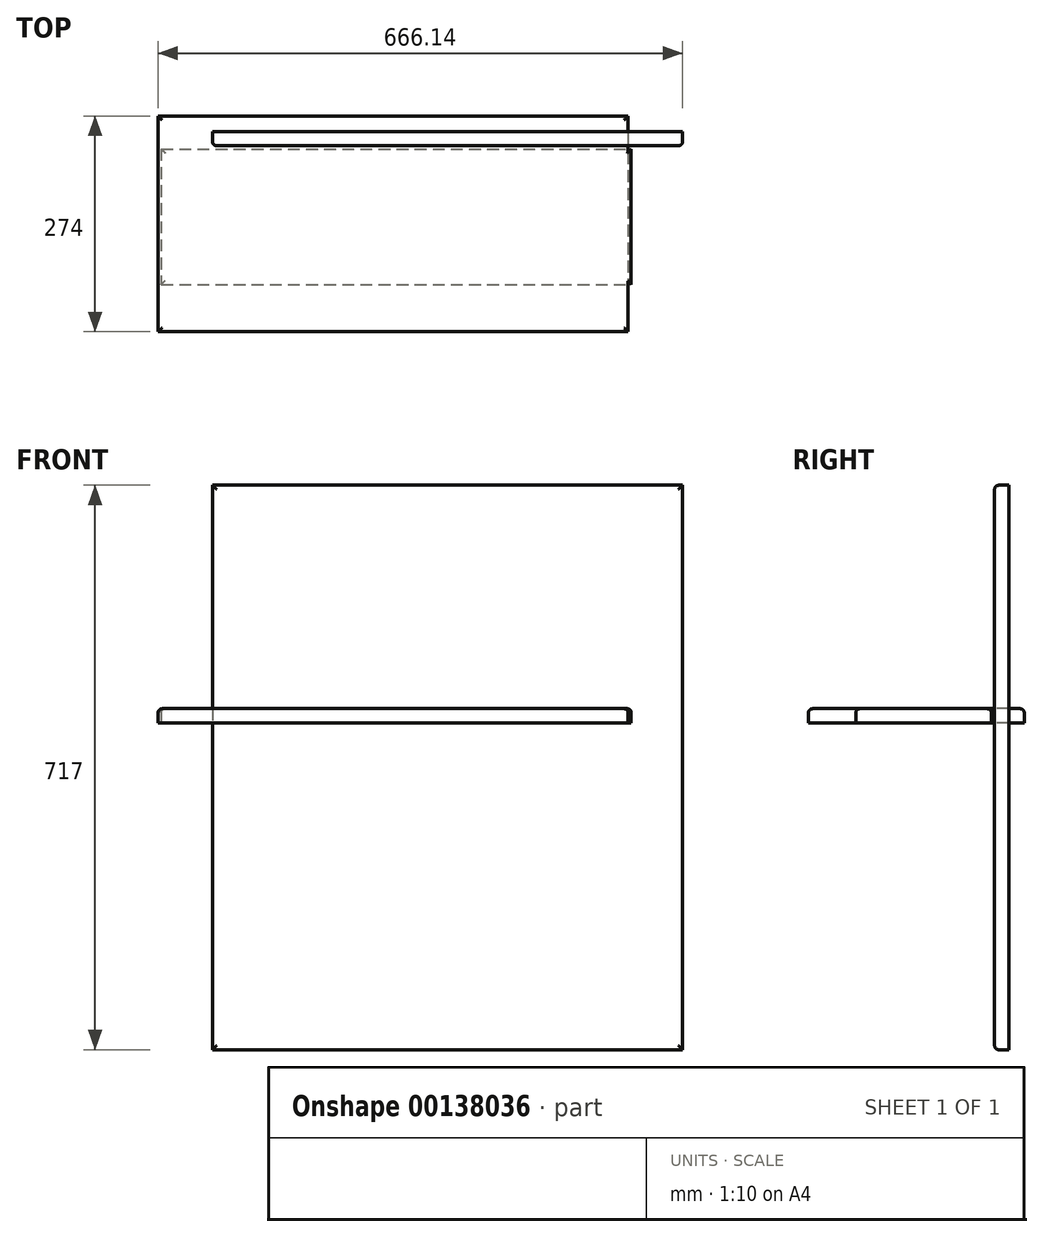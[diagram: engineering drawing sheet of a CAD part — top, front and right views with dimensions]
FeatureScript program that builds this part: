
annotation { "Feature Type Name" : "Feature", "Feature Type Description" : "" }
export const myFeature = defineFeature(function(context is Context, id is Id, definition is map)
    precondition{}
    {
        {
            var Q0;
            Q0=qCreatedBy(makeId("Front.planeOp"),FACE);
            var sketch = newSketch(context, id + "F0", { "sketchPlane" : qUnion([Q0])});
            skLineSegment(sketch, "E0.bottom", {"start": v(-320.4, 301.85) * mm, "end": v(276.6, 301.85) * mm});
            skLineSegment(sketch, "E0.top", {"start": v(-320.4, -415.15) * mm, "end": v(276.6, -415.15) * mm});
            skLineSegment(sketch, "E0.left", {"start": v(-320.4, 301.85) * mm, "end": v(-320.4, -415.15) * mm});
            skLineSegment(sketch, "E0.right", {"start": v(276.6, 301.85) * mm, "end": v(276.6, -415.15) * mm});
            skSolve(sketch);
        }
        {
            var Q0;
            Q0 = qSketchRegion(id + "F0", true);
            extrude(context, id + "F1", {"entities" : qUnion([Q0]), "depth" : 18 * mm});
        }
        {
            var Q0;
            Q0=makeQuery(id+"F1.opExtrude","CAP_FACE",FACE,{"disambiguationData":[OSD([sQuery(id+"F0.wireOp",EDGE,"E0.bottom"),sQuery(id+"F0.wireOp",EDGE,"E0.top"),sQuery(id+"F0.wireOp",EDGE,"E0.left"),sQuery(id+"F0.wireOp",EDGE,"E0.right")])],"isStart":false});
            fillet(context, id + "F2", {"entities" : qUnion([Q0]), "radius" : 5 * mm, "tangentPropagation" : true, "allowEdgeOverflow" : false});
        }
        {
            var Q0;
            Q0=makeQuery(id+"F1.opExtrude","SWEPT_BODY",BODY,{"disambiguationData":[OSD([sQuery(id+"F0.wireOp",EDGE,"E0.bottom"),sQuery(id+"F0.wireOp",EDGE,"E0.top"),sQuery(id+"F0.wireOp",EDGE,"E0.left"),sQuery(id+"F0.wireOp",EDGE,"E0.right")])]});
            transform(context, id + "F3", {"entities" : qUnion([Q0]), "transformType" : TransformType.TRANSLATION_3D, "dx" : 700 * mm, "dy" : 0 * mm, "dz" : 0 * mm, "makeCopy" : true});
        }
        {
            var Q0;
            Q0=makeQuery(id+"F3.opPattern","COPY",FACE,{"derivedFrom":makeQuery(id+"F1.opExtrude","CAP_FACE",FACE,{"disambiguationData":[OSD([sQuery(id+"F0.wireOp",EDGE,"E0.bottom"),sQuery(id+"F0.wireOp",EDGE,"E0.top"),sQuery(id+"F0.wireOp",EDGE,"E0.left"),sQuery(id+"F0.wireOp",EDGE,"E0.right")])],"isStart":false}),"instanceName":"1"});
            var sketch = newSketch(context, id + "F4", { "sketchPlane" : qUnion([Q0])});
            skLineSegment(sketch, "E1.bottom", {"start": v(384.6, 296.85) * mm, "end": v(971.6, 296.85) * mm});
            skLineSegment(sketch, "E1.top", {"start": v(384.6, 124.85) * mm, "end": v(971.6, 124.85) * mm});
            skLineSegment(sketch, "E1.left", {"start": v(384.6, 296.85) * mm, "end": v(384.6, 124.85) * mm});
            skLineSegment(sketch, "E1.right", {"start": v(971.6, 296.85) * mm, "end": v(971.6, 124.85) * mm});
            skSolve(sketch);
        }
        {
            var Q0;
            Q0=makeQuery(id+"F4.imprint","IMPRINT",FACE,{"disambiguationData":[TD([[makeQuery(id+"F4.imprint","IMPRINT",EDGE,{"derivedFrom":sQuery(id+"F4.wireOp",EDGE,"E1.bottom")}),1.0]])]});
            extrude(context, id + "F5", {"entities" : qUnion([Q0]), "operationType" : NewBodyOperationType.ADD, "oppositeDirection" : true, "depth" : 17 * mm});
        }
        {
            var Q0;
            Q0=makeQuery(id+"F3.opPattern","COPY",BODY,{"derivedFrom":makeQuery(id+"F1.opExtrude","SWEPT_BODY",BODY,{"disambiguationData":[OSD([sQuery(id+"F0.wireOp",EDGE,"E0.bottom"),sQuery(id+"F0.wireOp",EDGE,"E0.top"),sQuery(id+"F0.wireOp",EDGE,"E0.left"),sQuery(id+"F0.wireOp",EDGE,"E0.right")])]}),"instanceName":"1"});
            deleteBodies(context, id + "F6", {"entities" : qUnion([Q0])});
        }
        {
            var Q0;
            Q0=qCreatedBy(makeId("Top.planeOp"),FACE);
            var sketch = newSketch(context, id + "F7", { "sketchPlane" : qUnion([Q0])});
            skLineSegment(sketch, "E2.bottom", {"start": v(-385.62, -22.21) * mm, "end": v(211.38, -22.21) * mm});
            skLineSegment(sketch, "E2.top", {"start": v(-385.62, -194.21) * mm, "end": v(211.38, -194.21) * mm});
            skLineSegment(sketch, "E2.left", {"start": v(-385.62, -22.21) * mm, "end": v(-385.62, -194.21) * mm});
            skLineSegment(sketch, "E2.right", {"start": v(211.38, -22.21) * mm, "end": v(211.38, -194.21) * mm});
            skSolve(sketch);
        }
        {
            var Q0;
            Q0 = qSketchRegion(id + "F7", true);
            extrude(context, id + "F8", {"entities" : qUnion([Q0]), "depth" : 18 * mm});
        }
        {
            var Q0;
            Q0=makeQuery(id+"F8.opExtrude","CAP_FACE",FACE,{"disambiguationData":[OSD([sQuery(id+"F7.wireOp",EDGE,"E2.bottom"),sQuery(id+"F7.wireOp",EDGE,"E2.top"),sQuery(id+"F7.wireOp",EDGE,"E2.left"),sQuery(id+"F7.wireOp",EDGE,"E2.right")])],"isStart":false});
            fillet(context, id + "F9", {"entities" : qUnion([Q0]), "radius" : 5 * mm, "tangentPropagation" : true, "allowEdgeOverflow" : false});
        }
        {
            var Q0;
            Q0=qCreatedBy(makeId("Top.planeOp"),FACE);
            var sketch = newSketch(context, id + "F10", { "sketchPlane" : qUnion([Q0])});
            skLineSegment(sketch, "E3.bottom", {"start": v(-389.54, 19.61) * mm, "end": v(207.46, 19.61) * mm});
            skLineSegment(sketch, "E3.top", {"start": v(-389.54, -254.39) * mm, "end": v(207.46, -254.39) * mm});
            skLineSegment(sketch, "E3.left", {"start": v(-389.54, 19.61) * mm, "end": v(-389.54, -254.39) * mm});
            skLineSegment(sketch, "E3.right", {"start": v(207.46, 19.61) * mm, "end": v(207.46, -254.39) * mm});
            skSolve(sketch);
        }
        {
            var Q0;
            Q0 = qSketchRegion(id + "F10", true);
            extrude(context, id + "F11", {"entities" : qUnion([Q0]), "depth" : 18 * mm});
        }
        {
            var Q0;
            Q0=makeQuery(id+"F11.opExtrude","CAP_EDGE",EDGE,{"disambiguationData":[OSD([sQuery(id+"F10.wireOp",EDGE,"E3.bottom")])],"isStart":false});
            var Q1;
            Q1=makeQuery(id+"F11.opExtrude","CAP_EDGE",EDGE,{"disambiguationData":[OSD([sQuery(id+"F10.wireOp",EDGE,"E3.left")])],"isStart":false});
            var Q2;
            Q2=makeQuery(id+"F11.opExtrude","CAP_EDGE",EDGE,{"disambiguationData":[OSD([sQuery(id+"F10.wireOp",EDGE,"E3.top")])],"isStart":false});
            var Q3;
            Q3=makeQuery(id+"F11.opExtrude","CAP_EDGE",EDGE,{"disambiguationData":[OSD([sQuery(id+"F10.wireOp",EDGE,"E3.right")])],"isStart":false});
            fillet(context, id + "F12", {"entities" : qUnion([Q0, Q1, Q2, Q3]), "radius" : 5 * mm, "tangentPropagation" : true, "allowEdgeOverflow" : false});
        }
    });
